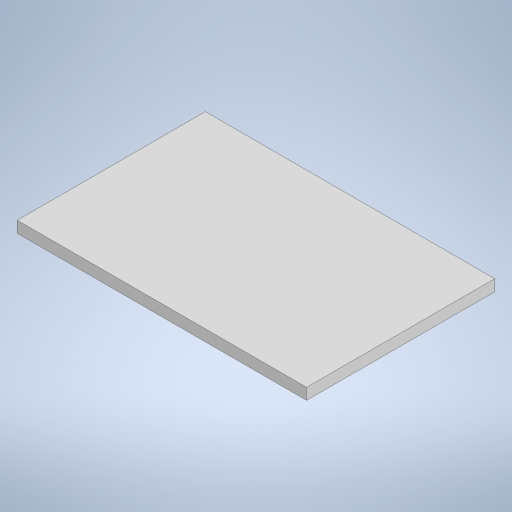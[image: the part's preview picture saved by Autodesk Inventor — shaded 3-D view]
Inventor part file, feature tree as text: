
AUTODESK INVENTOR PART (.ipt)
format: ipt  version: 2024 (Build 280153000, 153)  size: 201,216 bytes
history: native  units: mm
features: extrude x1, sketch x1
ambient origin geometry x8: Origin, YZ Plane, XZ Plane, XY Plane, X Axis, Y Axis, Z Axis, Center Point
bodies: Solid1 (feature_tree)
feature tree (2):
  extrude  "Extrusion1"  Depth=52.0mm
  sketch  "Sketch1"  dims[d0=80.0mm d1=52.0mm d2=3.125mm d3=0.0mm]
